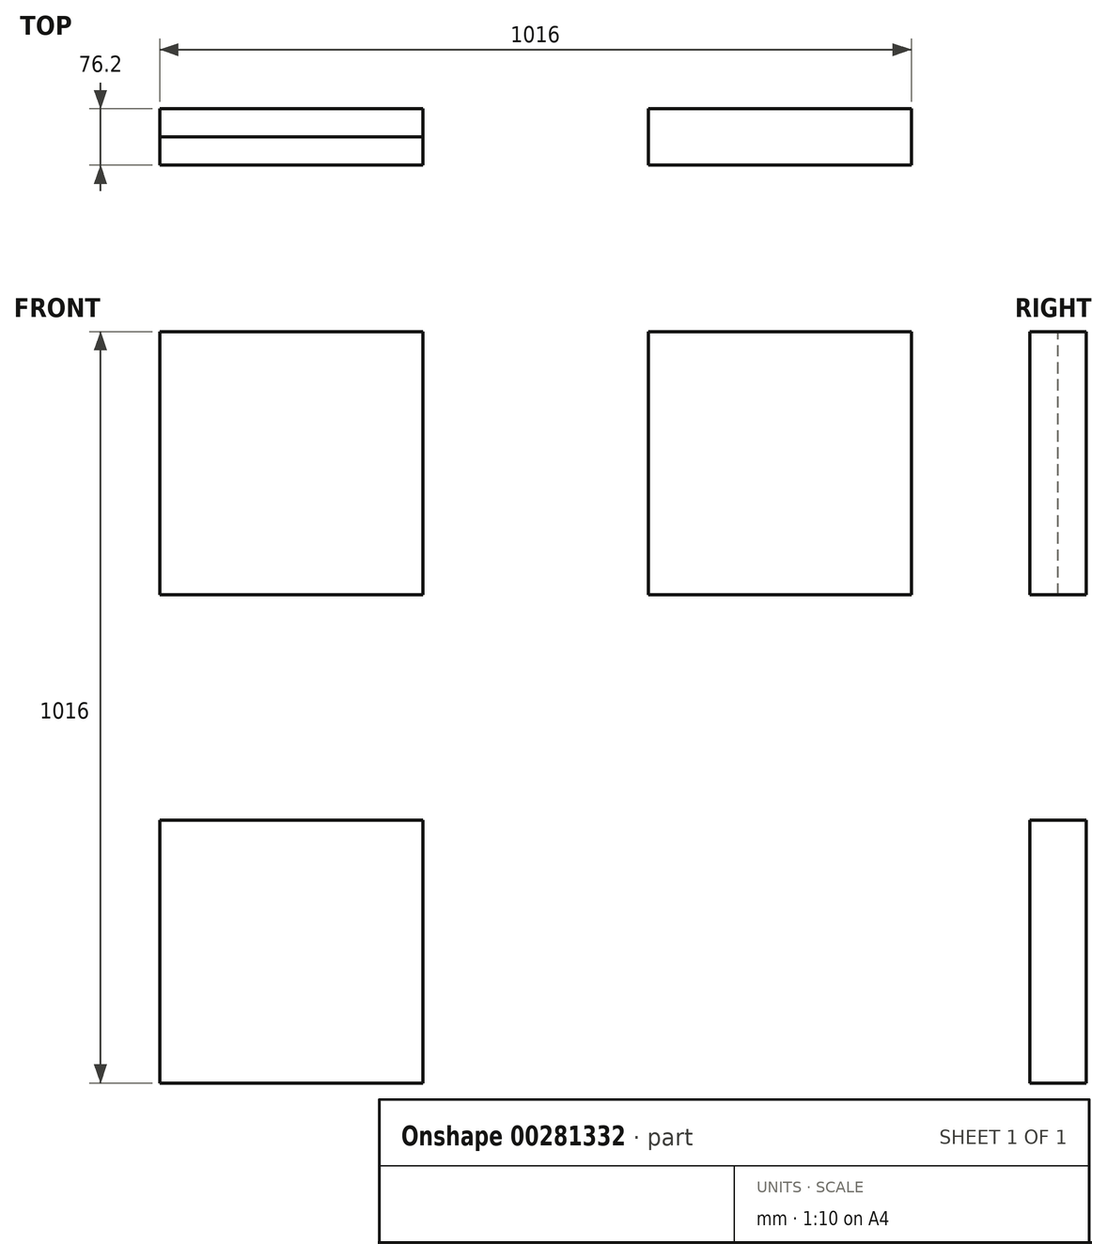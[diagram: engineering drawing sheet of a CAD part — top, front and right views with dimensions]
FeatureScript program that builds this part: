
annotation { "Feature Type Name" : "Feature", "Feature Type Description" : "" }
export const myFeature = defineFeature(function(context is Context, id is Id, definition is map)
    precondition{}
    {
        {
            var Q0;
            Q0=qCreatedBy(makeId("Front.planeOp"),FACE);
            var sketch = newSketch(context, id + "F0", { "sketchPlane" : qUnion([Q0])});
            skLineSegment(sketch, "E0", {"start": v(945.1, -4554.72) * mm, "end": v(945.1, -3538.72) * mm});
            skLineSegment(sketch, "E1", {"start": v(945.1, -3538.72) * mm, "end": v(1961.1, -3538.72) * mm});
            skLineSegment(sketch, "E2", {"start": v(1961.1, -3538.72) * mm, "end": v(1961.1, -4554.72) * mm});
            skLineSegment(sketch, "E3", {"start": v(1961.1, -4554.72) * mm, "end": v(945.1, -4554.72) * mm});
            skLineSegment(sketch, "E4", {"start": v(945.1, -3538.72) * mm, "end": v(1300.7, -3538.72) * mm});
            skLineSegment(sketch, "E5", {"start": v(1300.7, -3538.72) * mm, "end": v(1300.7, -3894.32) * mm});
            skLineSegment(sketch, "E6", {"start": v(1300.7, -4199.12) * mm, "end": v(1300.7, -4554.72) * mm});
            skLineSegment(sketch, "E7", {"start": v(1300.7, -4554.72) * mm, "end": v(945.1, -4554.72) * mm});
            skLineSegment(sketch, "E8", {"start": v(1961.1, -4554.72) * mm, "end": v(1605.5, -4554.72) * mm});
            skLineSegment(sketch, "E9", {"start": v(1605.5, -4554.72) * mm, "end": v(1605.5, -4199.12) * mm});
            skLineSegment(sketch, "E10", {"start": v(1605.5, -3894.32) * mm, "end": v(1605.5, -3538.72) * mm});
            skLineSegment(sketch, "E11", {"start": v(1605.5, -3538.72) * mm, "end": v(1961.1, -3538.72) * mm});
            skLineSegment(sketch, "E12", {"start": v(1961.1, -3538.72) * mm, "end": v(1961.1, -3894.32) * mm});
            skLineSegment(sketch, "E13", {"start": v(1961.1, -3894.32) * mm, "end": v(1605.5, -3894.32) * mm});
            skLineSegment(sketch, "E14", {"start": v(1300.7, -3894.32) * mm, "end": v(945.1, -3894.32) * mm});
            skLineSegment(sketch, "E15", {"start": v(945.1, -4199.12) * mm, "end": v(1300.7, -4199.12) * mm});
            skLineSegment(sketch, "E16", {"start": v(1605.5, -4199.12) * mm, "end": v(1961.1, -4199.12) * mm});
            skLineSegment(sketch, "E17", {"start": v(945.1, -3538.72) * mm, "end": v(945.1, -3894.32) * mm});
            skLineSegment(sketch, "E18", {"start": v(945.1, -4199.12) * mm, "end": v(945.1, -4554.72) * mm});
            skLineSegment(sketch, "E19", {"start": v(1961.1, -4554.72) * mm, "end": v(1961.1, -4199.12) * mm});
            skSolve(sketch);
        }
        {
            var Q0;
            Q0=makeQuery(id+"F0.imprint","IMPRINT",FACE,{"disambiguationData":[TD([[makeQuery(id+"F0.imprint","IMPRINT",EDGE,{"derivedFrom":sQuery(id+"F0.wireOp",EDGE,"E6")}),-1.0]])]});
            var Q1;
            Q1=makeQuery(id+"F0.imprint","IMPRINT",FACE,{"disambiguationData":[TD([[makeQuery(id+"F0.imprint","IMPRINT",EDGE,{"derivedFrom":sQuery(id+"F0.wireOp",EDGE,"E0")}),-1.0]])]});
            var Q2;
            Q2=makeQuery(id+"F0.imprint","IMPRINT",FACE,{"disambiguationData":[TD([[makeQuery(id+"F0.imprint","IMPRINT",EDGE,{"derivedFrom":sQuery(id+"F0.wireOp",EDGE,"E8")}),-1.0]])]});
            var Q3;
            Q3=makeQuery(id+"F0.imprint","IMPRINT",FACE,{"disambiguationData":[TD([[makeQuery(id+"F0.imprint","IMPRINT",EDGE,{"derivedFrom":sQuery(id+"F0.wireOp",EDGE,"E10")}),-1.0]])]});
            var Q4;
            Q4=makeQuery(id+"F0.imprint","IMPRINT",FACE,{"disambiguationData":[TD([[makeQuery(id+"F0.imprint","IMPRINT",EDGE,{"derivedFrom":sQuery(id+"F0.wireOp",EDGE,"E4")}),-1.0]])]});
            extrude(context, id + "F1", {"entities" : qUnion([Q0, Q1, Q2, Q3, Q4]), "depth" : 38.1 * mm});
        }
        {
            var Q0;
            Q0=makeQuery(id+"F0.imprint","IMPRINT",FACE,{"disambiguationData":[TD([[makeQuery(id+"F0.imprint","IMPRINT",EDGE,{"derivedFrom":sQuery(id+"F0.wireOp",EDGE,"E10")}),-1.0]])]});
            var Q1;
            Q1=makeQuery(id+"F0.imprint","IMPRINT",FACE,{"disambiguationData":[TD([[makeQuery(id+"F0.imprint","IMPRINT",EDGE,{"derivedFrom":sQuery(id+"F0.wireOp",EDGE,"E8")}),-1.0]])]});
            var Q2;
            Q2=makeQuery(id+"F0.imprint","IMPRINT",FACE,{"disambiguationData":[TD([[makeQuery(id+"F0.imprint","IMPRINT",EDGE,{"derivedFrom":sQuery(id+"F0.wireOp",EDGE,"E6")}),-1.0]])]});
            var Q3;
            Q3=makeQuery(id+"F0.imprint","IMPRINT",FACE,{"disambiguationData":[TD([[makeQuery(id+"F0.imprint","IMPRINT",EDGE,{"derivedFrom":sQuery(id+"F0.wireOp",EDGE,"E4")}),-1.0]])]});
            extrude(context, id + "F2", {"entities" : qUnion([Q0, Q1, Q2, Q3]), "operationType" : NewBodyOperationType.ADD, "depth" : 76.2 * mm});
        }
    });
